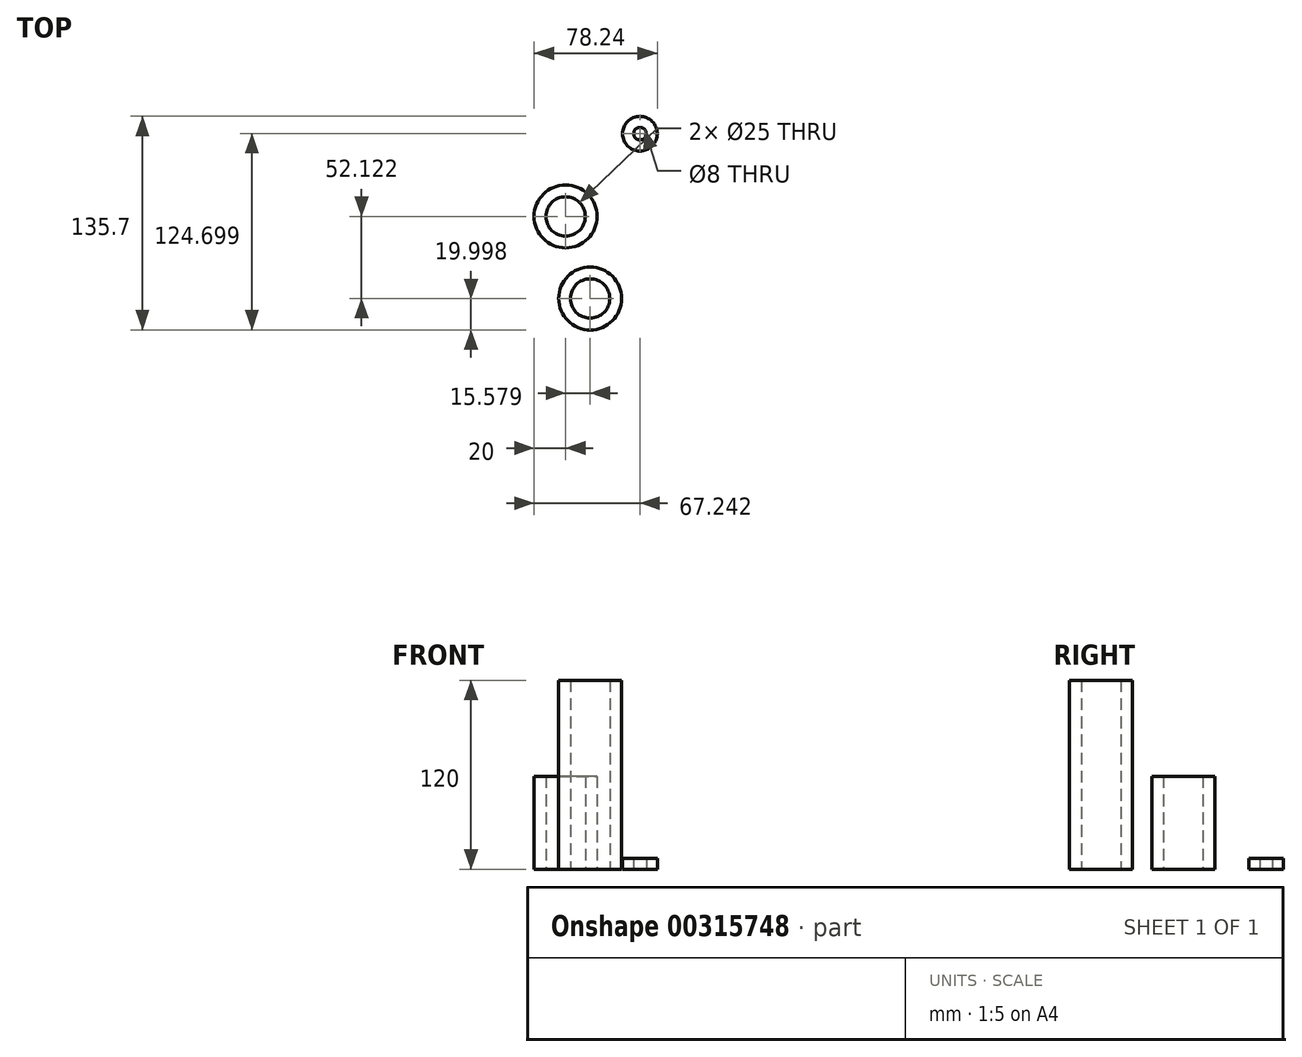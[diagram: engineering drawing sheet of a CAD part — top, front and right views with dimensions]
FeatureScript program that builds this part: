
annotation { "Feature Type Name" : "Feature", "Feature Type Description" : "" }
export const myFeature = defineFeature(function(context is Context, id is Id, definition is map)
    precondition{}
    {
        {
            var Q0;
            Q0=qCreatedBy(makeId("Top.planeOp"),FACE);
            var sketch = newSketch(context, id + "F0", { "sketchPlane" : qUnion([Q0])});
            skCircle(sketch, "E0", {"center": v(0, 0) * mm, "radius": 12.5 * mm});
            skCircle(sketch, "E1", {"center": v(0, 0) * mm, "radius": 20 * mm});
            skCircle(sketch, "E2", {"center": v(15.58, -52.12) * mm, "radius": 12.5 * mm});
            skCircle(sketch, "E3", {"center": v(15.58, -52.12) * mm, "radius": 20 * mm});
            skSolve(sketch);
        }
        {
            var Q0;
            Q0=makeQuery(id+"F0.imprint","IMPRINT",FACE,{"disambiguationData":[TD([[makeQuery(id+"F0.imprint","IMPRINT",EDGE,{"derivedFrom":sQuery(id+"F0.wireOp",EDGE,"E0")}),-1.0]])]});
            extrude(context, id + "F1", {"entities" : qUnion([Q0]), "depth" : 59 * mm});
        }
        {
            var Q0;
            Q0=qCreatedBy(makeId("Top.planeOp"),FACE);
            var sketch = newSketch(context, id + "F2", { "sketchPlane" : qUnion([Q0])});
            skCircle(sketch, "E4", {"center": v(47.24, 52.58) * mm, "radius": 11 * mm});
            skCircle(sketch, "E5", {"center": v(47.24, 52.58) * mm, "radius": 4 * mm});
            skSolve(sketch);
        }
        {
            var Q0;
            Q0=makeQuery(id+"F2.imprint","IMPRINT",FACE,{"disambiguationData":[TD([[makeQuery(id+"F2.imprint","IMPRINT",EDGE,{"derivedFrom":sQuery(id+"F2.wireOp",EDGE,"E4")}),1.0]])]});
            extrude(context, id + "F3", {"entities" : qUnion([Q0]), "depth" : 7 * mm});
        }
        {
            var Q0;
            Q0=makeQuery(id+"F0.imprint","IMPRINT",FACE,{"disambiguationData":[TD([[makeQuery(id+"F0.imprint","IMPRINT",EDGE,{"derivedFrom":sQuery(id+"F0.wireOp",EDGE,"E2")}),-1.0]])]});
            extrude(context, id + "F4", {"entities" : qUnion([Q0]), "depth" : 120 * mm});
        }
    });
